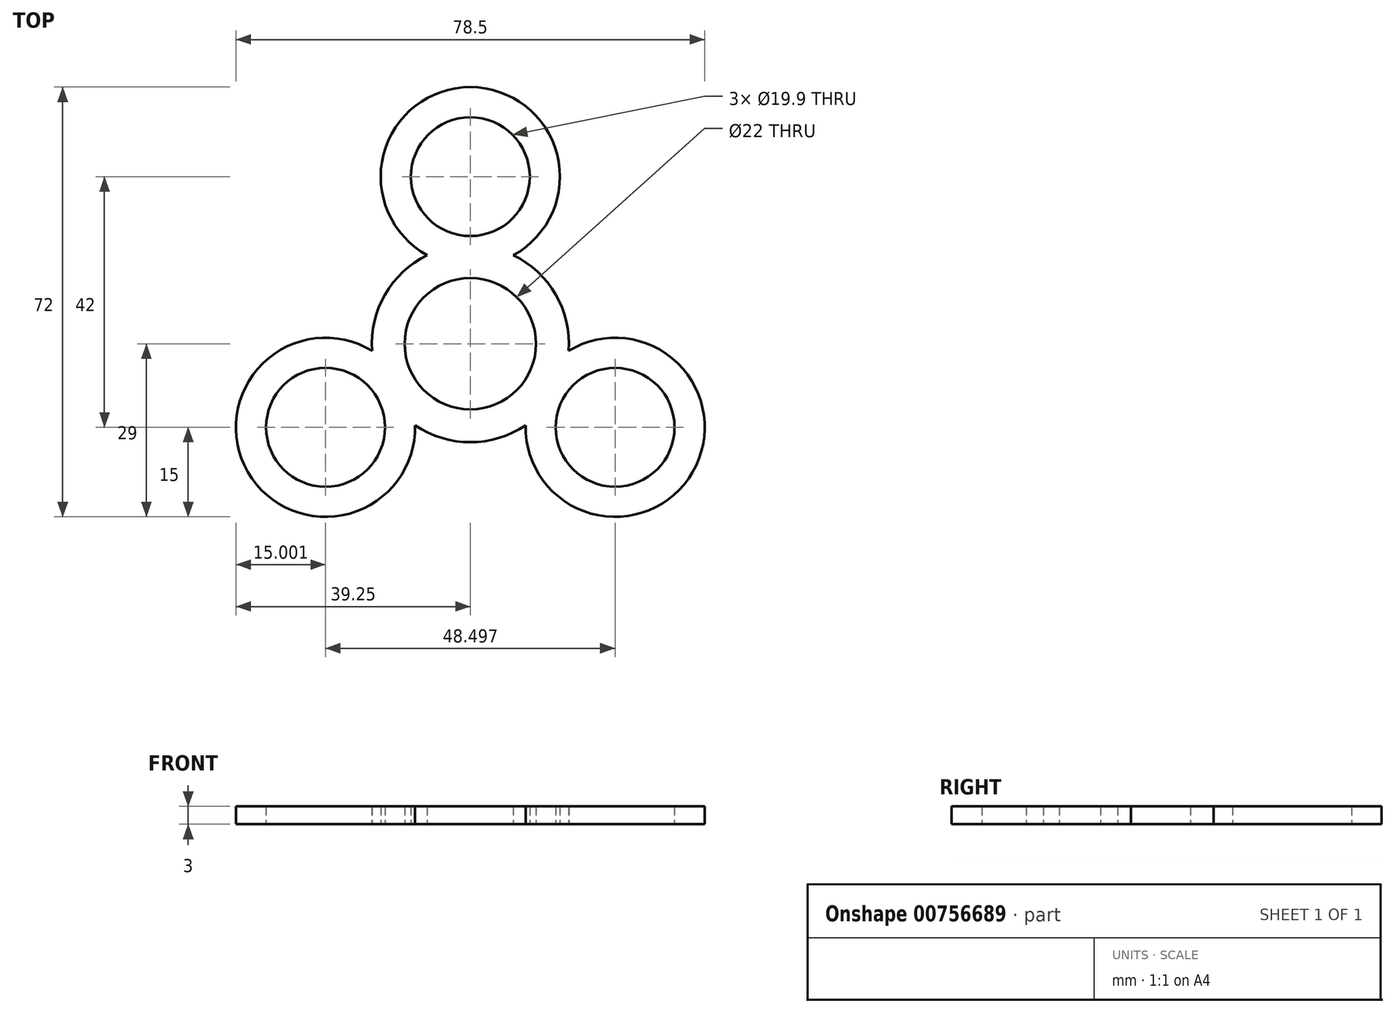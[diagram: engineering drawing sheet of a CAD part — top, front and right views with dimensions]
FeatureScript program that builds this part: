
annotation { "Feature Type Name" : "Feature", "Feature Type Description" : "" }
export const myFeature = defineFeature(function(context is Context, id is Id, definition is map)
    precondition{}
    {
        {
            var Q0;
            Q0=qCreatedBy(makeId("Top.planeOp"),FACE);
            var sketch = newSketch(context, id + "F0", { "sketchPlane" : qUnion([Q0])});
            skArc(sketch, "E0", {"start": v(9.53, 5.5) * mm, "mid": v(0, 11) * mm, "end": v(-9.53, 5.5) * mm});
            skLineSegment(sketch, "E1", {"start": v(0, 0) * mm, "end": v(0, 28) * mm});
            skCircle(sketch, "E2", {"center": v(0, 28) * mm, "radius": 9.95 * mm});
            skArc(sketch, "E3", {"start": v(7.2, 14.84) * mm, "mid": v(0, 43) * mm, "end": v(-7.2, 14.84) * mm});
            skArc(sketch, "E4", {"start": v(-7.2, 14.84) * mm, "mid": v(-11.24, 12.08) * mm, "end": v(-14.29, 8.25) * mm});
            skArc(sketch, "E5.trimOffspring", {"start": v(14.29, 8.25) * mm, "mid": v(11.24, 12.08) * mm, "end": v(7.2, 14.84) * mm});
            skCircle(sketch, "E6.1.0", {"center": v(-24.25, -14) * mm, "radius": 9.95 * mm});
            skArc(sketch, "E6.1.1", {"start": v(-16.46, -1.18) * mm, "mid": v(-37.24, -21.5) * mm, "end": v(-9.25, -13.66) * mm});
            skArc(sketch, "E6.1.2", {"start": v(-14.29, 8.25) * mm, "mid": v(-16.08, 3.7) * mm, "end": v(-16.46, -1.18) * mm});
            skArc(sketch, "E6.1.3", {"start": v(-9.53, 5.5) * mm, "mid": v(-9.53, -5.5) * mm, "end": v(0, -11) * mm});
            skArc(sketch, "E6.1.4", {"start": v(-9.25, -13.66) * mm, "mid": v(-4.84, -15.77) * mm, "end": v(0, -16.5) * mm});
            skCircle(sketch, "E6.2.0", {"center": v(24.25, -14) * mm, "radius": 9.95 * mm});
            skArc(sketch, "E6.2.1", {"start": v(9.25, -13.66) * mm, "mid": v(37.24, -21.5) * mm, "end": v(16.46, -1.18) * mm});
            skArc(sketch, "E6.2.2", {"start": v(0, -16.5) * mm, "mid": v(4.84, -15.77) * mm, "end": v(9.25, -13.66) * mm});
            skArc(sketch, "E6.2.3", {"start": v(0, -11) * mm, "mid": v(9.53, -5.5) * mm, "end": v(9.53, 5.5) * mm});
            skArc(sketch, "E6.2.4", {"start": v(16.46, -1.18) * mm, "mid": v(16.08, 3.7) * mm, "end": v(14.29, 8.25) * mm});
            skSolve(sketch);
        }
        {
            var Q0;
            Q0=makeQuery(id+"F0.imprint","IMPRINT",FACE,{"disambiguationData":[TD([[makeQuery(id+"F0.imprint","IMPRINT",EDGE,{"derivedFrom":sQuery(id+"F0.wireOp",EDGE,"E2")}),-1.0]])]});
            extrude(context, id + "F1", {"entities" : qUnion([Q0]), "depth" : 3 * mm, "offsetDistance" : 25 * mm});
        }
    });
